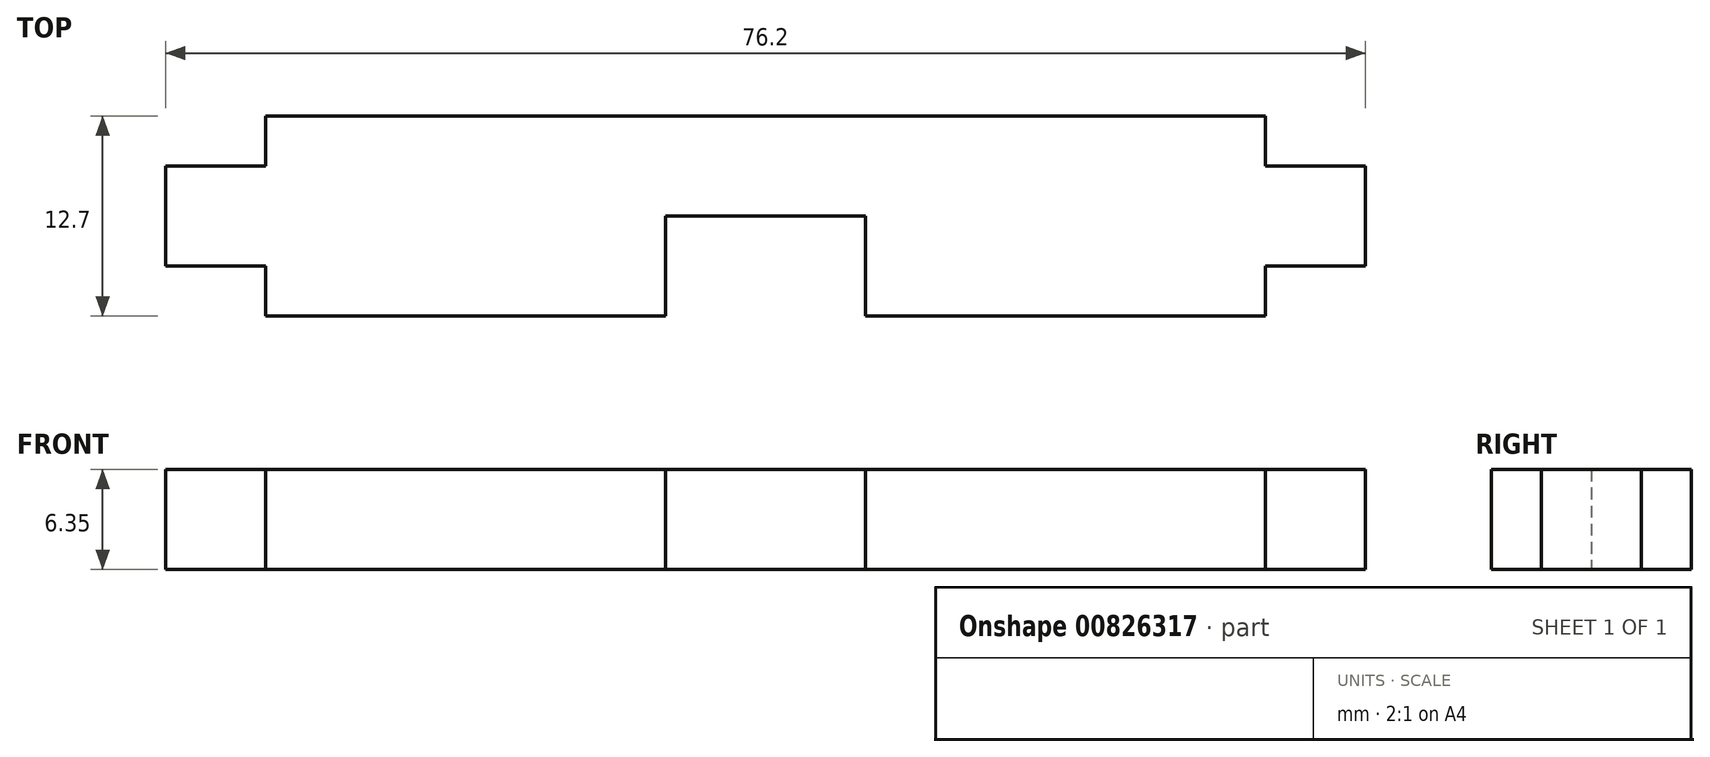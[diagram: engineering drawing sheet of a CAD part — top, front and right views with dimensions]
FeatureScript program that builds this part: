
annotation { "Feature Type Name" : "Feature", "Feature Type Description" : "" }
export const myFeature = defineFeature(function(context is Context, id is Id, definition is map)
    precondition{}
    {
        {
            var Q0;
            Q0=qCreatedBy(makeId("Top.planeOp"),FACE);
            var sketch = newSketch(context, id + "F0", { "sketchPlane" : qUnion([Q0])});
            skLineSegment(sketch, "E0.bottom", {"start": v(6.35, 0) * mm, "end": v(69.85, 0) * mm});
            skLineSegment(sketch, "E0.top", {"start": v(6.35, -12.7) * mm, "end": v(31.75, -12.7) * mm});
            skLineSegment(sketch, "E0.left", {"start": v(0, -3.17) * mm, "end": v(0, -9.52) * mm});
            skLineSegment(sketch, "E1", {"start": v(31.75, -12.7) * mm, "end": v(31.75, -6.35) * mm});
            skLineSegment(sketch, "E2", {"start": v(31.75, -6.35) * mm, "end": v(44.45, -6.35) * mm});
            skLineSegment(sketch, "E3", {"start": v(44.45, -6.35) * mm, "end": v(44.45, -12.7) * mm});
            skLineSegment(sketch, "E4", {"start": v(44.45, -12.7) * mm, "end": v(69.85, -12.7) * mm});
            skLineSegment(sketch, "E5", {"start": v(6.35, 0) * mm, "end": v(6.35, -3.17) * mm});
            skLineSegment(sketch, "E6", {"start": v(6.35, -3.17) * mm, "end": v(0, -3.17) * mm});
            skLineSegment(sketch, "E7", {"start": v(0, -9.52) * mm, "end": v(6.35, -9.52) * mm});
            skLineSegment(sketch, "E8", {"start": v(6.35, -9.52) * mm, "end": v(6.35, -12.7) * mm});
            skPoint(sketch, "E9.orphan", {"position": v(0, 0) * mm});
            skPoint(sketch, "E10.orphan", {"position": v(0, -12.7) * mm});
            skLineSegment(sketch, "E11", {"start": v(38.1, -6.35) * mm, "end": v(38.1, -7.62) * mm, "construction": true});
            skLineSegment(sketch, "E12.MirrorCS", {"start": v(69.85, 0) * mm, "end": v(69.85, -3.17) * mm});
            skLineSegment(sketch, "E13.MirrorCS", {"start": v(69.85, -3.17) * mm, "end": v(76.2, -3.17) * mm});
            skLineSegment(sketch, "E14.MirrorCS", {"start": v(76.2, -3.17) * mm, "end": v(76.2, -9.52) * mm});
            skLineSegment(sketch, "E15.MirrorCS", {"start": v(76.2, -9.52) * mm, "end": v(69.85, -9.52) * mm});
            skLineSegment(sketch, "E16.MirrorCS", {"start": v(69.85, -9.52) * mm, "end": v(69.85, -12.7) * mm});
            skSolve(sketch);
        }
        {
            var Q0;
            Q0=makeQuery(id+"F0.imprint","IMPRINT",FACE,{"disambiguationData":[TD([[makeQuery(id+"F0.imprint","IMPRINT",EDGE,{"derivedFrom":sQuery(id+"F0.wireOp",EDGE,"E0.bottom")}),-1.0]])]});
            extrude(context, id + "F1", {"entities" : qUnion([Q0]), "depth" : 6.35 * mm, "offsetDistance" : 25.4 * mm});
        }
    });
